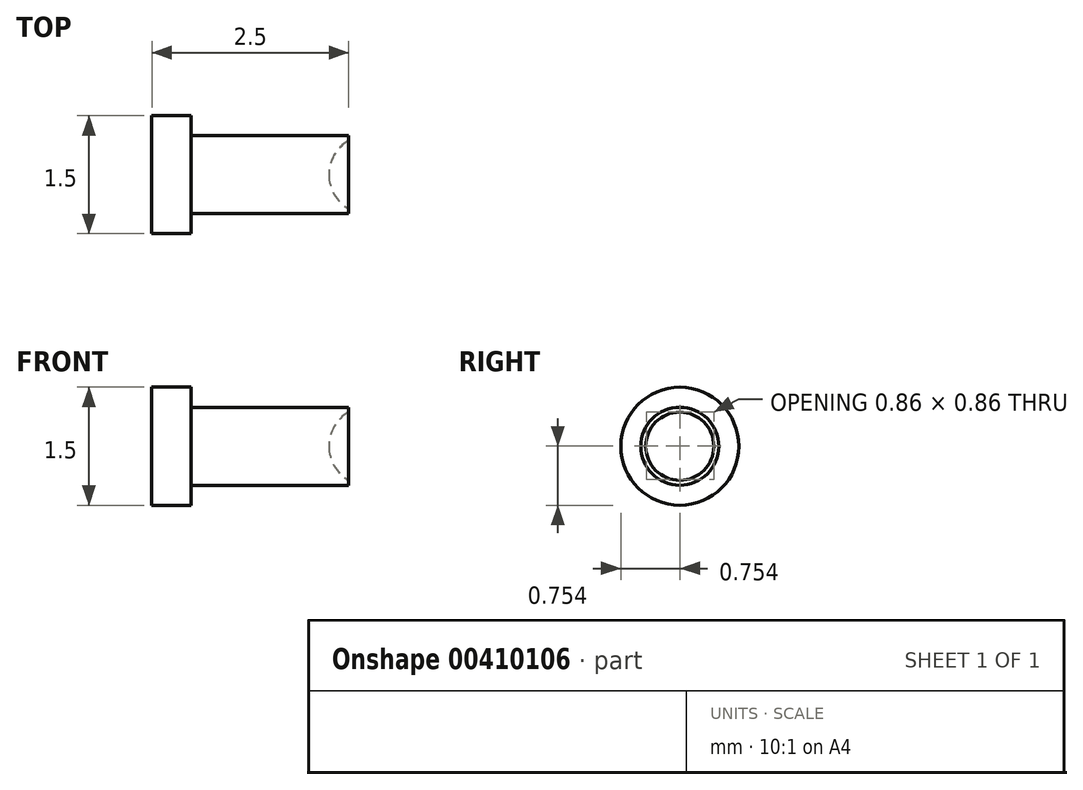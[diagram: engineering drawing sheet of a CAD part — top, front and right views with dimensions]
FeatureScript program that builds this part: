
annotation { "Feature Type Name" : "Feature", "Feature Type Description" : "" }
export const myFeature = defineFeature(function(context is Context, id is Id, definition is map)
    precondition{}
    {
        {
            var Q0;
            Q0=qCreatedBy(makeId("Top.planeOp"),FACE);
            var sketch = newSketch(context, id + "F0", { "sketchPlane" : qUnion([Q0])});
            skLineSegment(sketch, "E0", {"start": v(-1.13, 0) * mm, "end": v(1.6, 0) * mm, "construction": true});
            skLineSegment(sketch, "E1", {"start": v(-1.13, 0) * mm, "end": v(-1.13, 0.75) * mm});
            skLineSegment(sketch, "E2", {"start": v(-1.13, 0.75) * mm, "end": v(-0.63, 0.75) * mm});
            skLineSegment(sketch, "E3", {"start": v(-0.63, 0.75) * mm, "end": v(-0.63, 0.5) * mm});
            skLineSegment(sketch, "E4", {"start": v(-0.63, 0.5) * mm, "end": v(1.37, 0.5) * mm});
            skLineSegment(sketch, "E5", {"start": v(1.37, 0.5) * mm, "end": v(1.37, 0.43) * mm});
            skLineSegment(sketch, "E6", {"start": v(1.12, 0) * mm, "end": v(-1.13, 0) * mm});
            skArc(sketch, "E7", {"start": v(1.37, 0.43) * mm, "mid": v(1.19, 0.25) * mm, "end": v(1.12, 0) * mm});
            skPoint(sketch, "E8.orphan", {"position": v(1.37, 0) * mm});
            skSolve(sketch);
        }
        {
            var Q0;
            Q0=makeQuery(id+"F0.imprint","IMPRINT",FACE,{"disambiguationData":[TD([[makeQuery(id+"F0.imprint","IMPRINT",EDGE,{"derivedFrom":sQuery(id+"F0.wireOp",EDGE,"E1")}),-1.0]])]});
            var Q1;
            Q1=sQuery(id+"F0.wireOp",EDGE,"E0");
            revolve(context, id + "F1", {"entities" : qUnion([Q0]), "axis" : qUnion([Q1]), "revolveType" : RevolveType.FULL});
        }
    });
